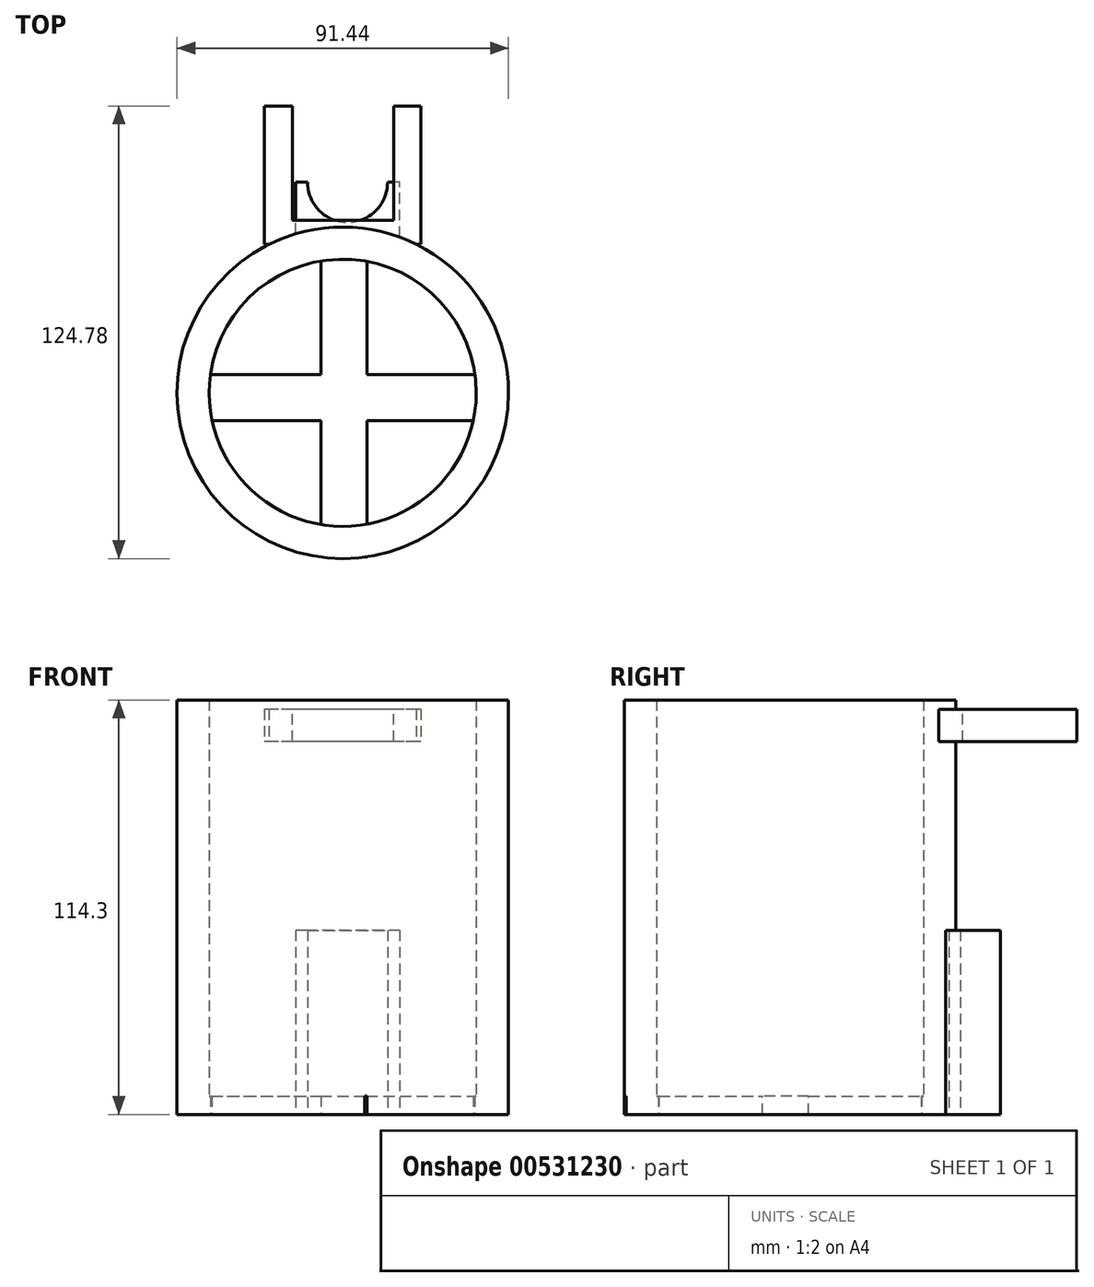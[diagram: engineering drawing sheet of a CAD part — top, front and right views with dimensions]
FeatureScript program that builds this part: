
annotation { "Feature Type Name" : "Feature", "Feature Type Description" : "" }
export const myFeature = defineFeature(function(context is Context, id is Id, definition is map)
    precondition{}
    {
        {
            var Q0;
            Q0=qCreatedBy(makeId("Top.planeOp"),FACE);
            var sketch = newSketch(context, id + "F0", { "sketchPlane" : qUnion([Q0])});
            skCircle(sketch, "E0", {"center": v(0, 0) * mm, "radius": 45.72 * mm});
            skSolve(sketch);
        }
        {
            var Q0;
            Q0=qCreatedBy(makeId("Top.planeOp"),FACE);
            var sketch = newSketch(context, id + "F1", { "sketchPlane" : qUnion([Q0])});
            skCircle(sketch, "E1", {"center": v(0, 0) * mm, "radius": 36.83 * mm});
            skSolve(sketch);
        }
        {
            var Q0;
            Q0=makeQuery(id+"F0.imprint","IMPRINT",FACE,{"disambiguationData":[TD([[makeQuery(id+"F0.imprint","IMPRINT",EDGE,{"derivedFrom":sQuery(id+"F0.wireOp",EDGE,"E0")}),1.0]])]});
            extrude(context, id + "F2", {"entities" : qUnion([Q0]), "depth" : 114.3 * mm, "offsetDistance" : 25.4 * mm});
        }
        {
            var Q0;
            Q0 = qSketchRegion(id + "F1", true);
            extrude(context, id + "F3", {"entities" : qUnion([Q0]), "operationType" : NewBodyOperationType.REMOVE, "depth" : 114.3 * mm, "offsetDistance" : 25.4 * mm});
        }
        {
            var Q0;
            Q0=qCreatedBy(makeId("Top.planeOp"),FACE);
            var sketch = newSketch(context, id + "F4", { "sketchPlane" : qUnion([Q0])});
            skLineSegment(sketch, "E2.bottom", {"start": v(-45.08, 5.06) * mm, "end": v(45.08, 5.06) * mm});
            skLineSegment(sketch, "E2.top", {"start": v(-45.08, -7.64) * mm, "end": v(45.08, -7.64) * mm});
            skLineSegment(sketch, "E2.left", {"start": v(-45.08, 5.06) * mm, "end": v(-45.08, -7.64) * mm});
            skLineSegment(sketch, "E2.right", {"start": v(45.08, 5.06) * mm, "end": v(45.08, -7.64) * mm});
            skSolve(sketch);
        }
        {
            var Q0;
            Q0=makeQuery(id+"F4.imprint","IMPRINT",FACE,{"disambiguationData":[TD([[makeQuery(id+"F4.imprint","IMPRINT",EDGE,{"derivedFrom":sQuery(id+"F4.wireOp",EDGE,"E2.bottom")}),-1.0]])]});
            extrude(context, id + "F5", {"entities" : qUnion([Q0]), "operationType" : NewBodyOperationType.ADD, "depth" : 5.08 * mm, "offsetDistance" : 25.4 * mm});
        }
        {
            var Q0;
            Q0=qCreatedBy(makeId("Top.planeOp"),FACE);
            var sketch = newSketch(context, id + "F6", { "sketchPlane" : qUnion([Q0])});
            skLineSegment(sketch, "E3.bottom", {"start": v(-6.03, -45.32) * mm, "end": v(6.67, -45.32) * mm});
            skLineSegment(sketch, "E3.top", {"start": v(-6.03, 45.32) * mm, "end": v(6.67, 45.32) * mm});
            skLineSegment(sketch, "E3.left", {"start": v(-6.03, -45.32) * mm, "end": v(-6.03, 45.32) * mm});
            skLineSegment(sketch, "E3.right", {"start": v(6.67, -45.32) * mm, "end": v(6.67, 45.32) * mm});
            skSolve(sketch);
        }
        {
            var Q0;
            Q0 = qSketchRegion(id + "F6", true);
            extrude(context, id + "F7", {"entities" : qUnion([Q0]), "operationType" : NewBodyOperationType.ADD, "depth" : 5.08 * mm, "offsetDistance" : 25.4 * mm});
        }
        {
            var Q0;
            Q0=qCreatedBy(makeId("Right.planeOp"),FACE);
            var sketch = newSketch(context, id + "F8", { "sketchPlane" : qUnion([Q0])});
            skLineSegment(sketch, "E4.bottom", {"start": v(40.96, 111.76) * mm, "end": v(79.06, 111.76) * mm});
            skLineSegment(sketch, "E4.top", {"start": v(40.96, 102.86) * mm, "end": v(79.06, 102.86) * mm});
            skLineSegment(sketch, "E4.left", {"start": v(40.96, 111.76) * mm, "end": v(40.96, 102.86) * mm});
            skLineSegment(sketch, "E4.right", {"start": v(79.06, 111.76) * mm, "end": v(79.06, 102.86) * mm});
            skLineSegment(sketch, "E5.bottom", {"start": v(67.63, 102.86) * mm, "end": v(79.06, 102.86) * mm});
            skLineSegment(sketch, "E5.top", {"start": v(67.63, 59.6) * mm, "end": v(79.06, 59.6) * mm});
            skLineSegment(sketch, "E5.left", {"start": v(67.63, 102.86) * mm, "end": v(67.63, 59.6) * mm});
            skLineSegment(sketch, "E5.right", {"start": v(79.06, 102.86) * mm, "end": v(79.06, 59.6) * mm});
            skSolve(sketch);
        }
        {
            var Q0;
            Q0=makeQuery(id+"F8.imprint","IMPRINT",FACE,{"disambiguationData":[TD([[makeQuery(id+"F8.imprint","IMPRINT",EDGE,{"derivedFrom":sQuery(id+"F8.wireOp",EDGE,"E4.bottom")}),-1.0]])]});
            var Q1;
            Q1=makeQuery(id+"F8.imprint","IMPRINT",FACE,{"disambiguationData":[TD([[makeQuery(id+"F8.imprint","IMPRINT",EDGE,{"derivedFrom":sQuery(id+"F8.wireOp",EDGE,"E5.bottom")}),-1.0]])]});
            extrude(context, id + "F9", {"entities" : qUnion([Q0, Q1]), "operationType" : NewBodyOperationType.ADD, "endBound" : BoundingType.SYMMETRIC, "depth" : 43.18 * mm, "offsetDistance" : 25.4 * mm});
        }
        {
            var Q0;
            Q0=qCreatedBy(makeId("Top.planeOp"),FACE);
            var sketch = newSketch(context, id + "F10", { "sketchPlane" : qUnion([Q0])});
            skLineSegment(sketch, "E6.bottom", {"start": v(15.74, 40.47) * mm, "end": v(-13.04, 40.47) * mm});
            skLineSegment(sketch, "E6.top", {"start": v(15.74, 58.05) * mm, "end": v(-13.04, 58.05) * mm});
            skLineSegment(sketch, "E6.left", {"start": v(15.74, 40.47) * mm, "end": v(15.74, 58.05) * mm});
            skLineSegment(sketch, "E6.right", {"start": v(-13.04, 40.47) * mm, "end": v(-13.04, 58.05) * mm});
            skCircle(sketch, "E7", {"center": v(1.35, 58.05) * mm, "radius": 11.04 * mm});
            skSolve(sketch);
        }
        {
            var Q0;
            Q0=makeQuery(id+"F10.imprint","IMPRINT",FACE,{"disambiguationData":[TD([[makeQuery(id+"F10.imprint","IMPRINT",EDGE,{"derivedFrom":sQuery(id+"F10.wireOp",EDGE,"E6.bottom")}),-1.0]])]});
            extrude(context, id + "F11", {"entities" : qUnion([Q0]), "operationType" : NewBodyOperationType.ADD, "depth" : 50.8 * mm, "offsetDistance" : 25.4 * mm});
        }
        {
            var Q0;
            Q0=makeQuery(id+"F9.opExtrude","SWEPT_FACE",FACE,{"disambiguationData":[OSD([sQuery(id+"F8.wireOp",EDGE,"E4.bottom")])]});
            var sketch = newSketch(context, id + "F12", { "sketchPlane" : qUnion([Q0])});
            skLineSegment(sketch, "E8.bottom", {"start": v(14.07, 47.55) * mm, "end": v(-13.87, 47.55) * mm});
            skLineSegment(sketch, "E8.top", {"start": v(14.07, 79.06) * mm, "end": v(-13.87, 79.06) * mm});
            skLineSegment(sketch, "E8.left", {"start": v(14.07, 47.55) * mm, "end": v(14.07, 79.06) * mm});
            skLineSegment(sketch, "E8.right", {"start": v(-13.87, 47.55) * mm, "end": v(-13.87, 79.06) * mm});
            skSolve(sketch);
        }
        {
            var Q0;
            Q0=makeQuery(id+"F12.imprint","IMPRINT",FACE,{"disambiguationData":[TD([[makeQuery(id+"F12.imprint","IMPRINT",EDGE,{"derivedFrom":sQuery(id+"F12.wireOp",EDGE,"E8.bottom")}),-1.0]])]});
            extrude(context, id + "F13", {"entities" : qUnion([Q0]), "operationType" : NewBodyOperationType.REMOVE, "oppositeDirection" : true, "depth" : 55.88 * mm, "offsetDistance" : 25.4 * mm});
        }
    });
